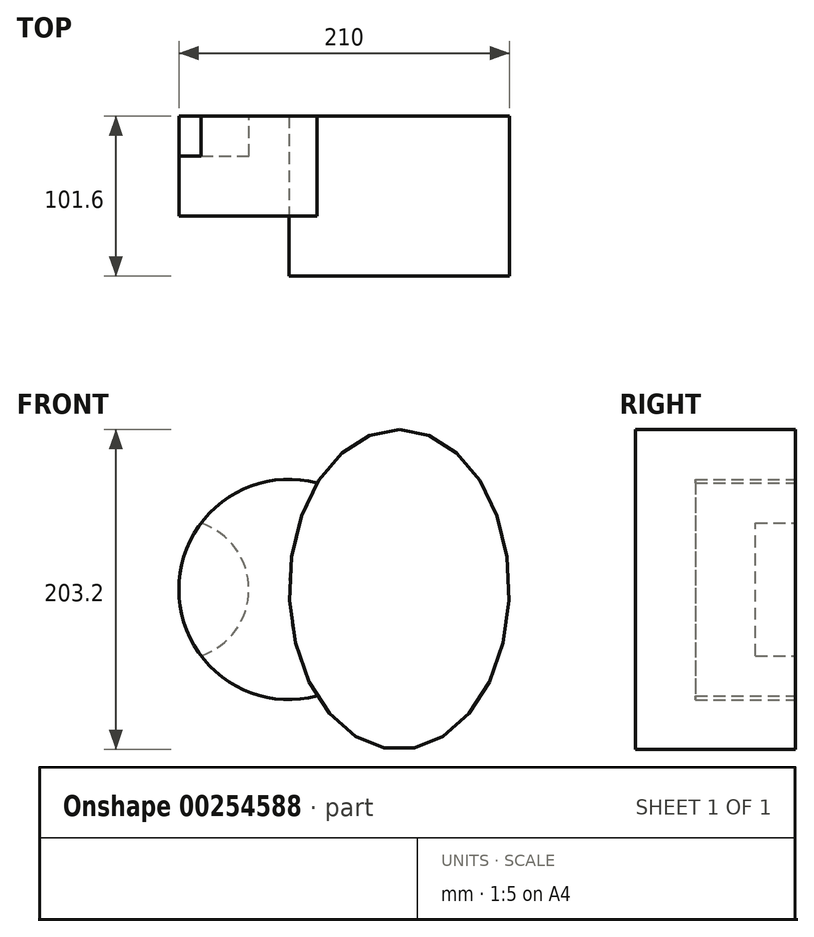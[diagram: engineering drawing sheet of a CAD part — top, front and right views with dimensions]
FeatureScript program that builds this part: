
annotation { "Feature Type Name" : "Feature", "Feature Type Description" : "" }
export const myFeature = defineFeature(function(context is Context, id is Id, definition is map)
    precondition{}
    {
        {
            var Q0;
            Q0=qCreatedBy(makeId("Front.planeOp"),FACE);
            var sketch = newSketch(context, id + "F0", { "sketchPlane" : qUnion([Q0])});
            skCircle(sketch, "E0", {"center": v(-70, 0) * mm, "radius": 44.45 * mm});
            skLineSegment(sketch, "E1", {"start": v(-25.55, 0) * mm, "end": v(-63.65, 0) * mm});
            skCircle(sketch, "E2", {"center": v(0, 0) * mm, "radius": 70 * mm});
            skLineSegment(sketch, "E3", {"start": v(70, 0) * mm, "end": v(70, 101.6) * mm});
            skEllipse(sketch, "E4", {"center": v(70, 0) * mm, "majorRadius": 101.6 * mm, "minorRadius": 70 * mm, "majorAxis": v(0, 1)});
            skSolve(sketch);
        }
        {
            var Q0;
            {var subQ0=sQuery(id+"F0.wireOp",EDGE,"E2");var subQ1=sQuery(id+"F0.wireOp",EDGE,"E0");var subQ2=makeQuery(id+"F0.imprint","INTERSECT",VERTEX,{"disambiguationData":[OD(0.0)],"derivedFrom":[subQ1,subQ0]});Q0=makeQuery(id+"F0.imprint","IMPRINT",FACE,{"disambiguationData":[TD([[makeQuery(id+"F0.imprint","IMPRINT",EDGE,{"disambiguationData":[TD([[subQ2,-1.0]])],"derivedFrom":subQ1}),1.0]])]});}
            extrude(context, id + "F1", {"entities" : qUnion([Q0]), "depth" : 25.4 * mm});
        }
        {
            var Q0;
            {var subQ0=sQuery(id+"F0.wireOp",EDGE,"E0");var subQ1=makeQuery(id+"F0.imprint","IMPRINT",VERTEX,{"derivedFrom":subQ0});Q0=makeQuery(id+"F0.imprint","IMPRINT",FACE,{"disambiguationData":[TD([[makeQuery(id+"F0.imprint","IMPRINT",EDGE,{"disambiguationData":[TD([[subQ1,-1.0]])],"derivedFrom":subQ0}),1.0]])]});}
            var Q1;
            {var subQ1=sQuery(id+"F0.wireOp",EDGE,"E0");var subQ7=makeQuery(id+"F0.imprint","IMPRINT",VERTEX,{"derivedFrom":subQ1});Q1=makeQuery(id+"F0.imprint","IMPRINT",FACE,{"disambiguationData":[TD([[makeQuery(id+"F0.imprint","IMPRINT",EDGE,{"disambiguationData":[TD([[subQ7,-1.0]])],"derivedFrom":subQ1}),-1.0]])]});}
            extrude(context, id + "F2", {"entities" : qUnion([Q0, Q1]), "depth" : 63.5 * mm});
        }
        {
            var Q0;
            {var subQ0=sQuery(id+"F0.wireOp",EDGE,"E3");Q0=makeQuery(id+"F0.imprint","IMPRINT",FACE,{"disambiguationData":[TD([[makeQuery(id+"F0.imprint","IMPRINT",EDGE,{"derivedFrom":subQ0}),-1.0]])]});}
            var Q1;
            {var subQ0=sQuery(id+"F0.wireOp",EDGE,"E2");var subQ1=makeQuery(id+"F0.imprint","INTERSECT",VERTEX,{"derivedFrom":[subQ0,sQuery(id+"F0.wireOp",EDGE,"E3")]});Q1=makeQuery(id+"F0.imprint","IMPRINT",FACE,{"disambiguationData":[TD([[makeQuery(id+"F0.imprint","IMPRINT",EDGE,{"disambiguationData":[TD([[subQ1,-1.0]])],"derivedFrom":subQ0}),1.0]])]});}
            var Q2;
            {var subQ0=sQuery(id+"F0.wireOp",EDGE,"E3");Q2=makeQuery(id+"F0.imprint","IMPRINT",FACE,{"disambiguationData":[TD([[makeQuery(id+"F0.imprint","IMPRINT",EDGE,{"derivedFrom":subQ0}),1.0]])]});}
            extrude(context, id + "F3", {"entities" : qUnion([Q0, Q1, Q2]), "depth" : 101.6 * mm});
        }
    });
